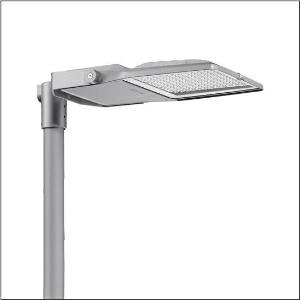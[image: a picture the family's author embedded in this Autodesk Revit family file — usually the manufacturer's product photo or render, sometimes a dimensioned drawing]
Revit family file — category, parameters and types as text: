
# Revit family: floodlight_fl_21_iq_midi___pl33t_5xa7782e2f3a_552b
name_source: partatom
category: Lighting Fixtures
units: mm (PartAtom-declared; Revit-internal decimal feet)

## family parameters
Cut with Voids When Loaded = No
Host = Face
Light Source = No
Part Type = Normal
Room Calculation Point = No
Round Connector Dimension = Use Diameter
Shared = No

## types (1)
- --- (1 x LED, 26540 lm, 208.1 W, 3000K)
    Apparent Load = 208 VA
    CIE Flux Codes = 26 75 99 100 100
    Color Rendering = 70
    Color Temperature = 3000K
    Default Elevation = 1800 mm
    Description = Floodlight FL 21 iQ midi, floodlight, primary light control with lens, of PMMA, primary optical cover: protective disc, of toughened safety glass, transparent, light distribution: PL33T, light emission: direct distribution, installation type: surface-mounted, LED, High Power LED, rated luminous flux: 26.540lm, luminous efficacy: 128lm/W, light colour: 730, colour temperature: 3000K, control gear: ECG iQ, control: optimised constant luminous flux control (CLO 2.0), Desk-Remote (wireless, voltage-free reading and setting of iQ features in the workshop via application-optimized NFC function/RFID function), Smart-Wire, Night-Set, Temp-Guard, Auto-Match, Street-Remote, with terminal, 6-pole, mains connection: 220..240V, AC, 50/60Hz, start of lifetime: 208W, end of service life: 227W, reduction: 90W, luminaire housing, of diecast aluminium, powder-coated, Siteco® metallic grey (DB 702S), corrosivity category C5 mid according to DIN EN ISO 12944, sealing non-destructively replaceable, please order mast flange separately, mast bracket, of steel, galvanised, powder-coated, Siteco® metallic grey (DB 702S), protection rating (complete): IP66, insulation class (complete): insulation class II (safety insulation), certification: CE, protection symbol: D, impact resistance: IK08, permissible operating ambient temperature: -40..+40°C, permissible operating ambient temperature for outdoor applications: -40..+50°C, standard: DIN EN 12944, LABS conformity tested according to VDMA 24364:2018-05, packaging unit: 1 piece

Light Distribution: PL33T
    Height = 76 mm
    Lamp = 1 x LED
    Lamp Light Flux = 26540 lm
    Lamp Power = 208.1 W
    Lamp count = 1
    Length = 657 mm
    Luminous efficacy = 128 lm/W
    Manufacturer = Siteco
    ModVariant = No
    Model = 5XA7782E2F3A
    Number of Poles = 1
    OnlyDefault = Yes
    Power Factor = 1
    Product Name = Floodlight FL 21 iQ midi | PL33T
    Product group = floodlight | pylon annexe
    ProductGroupID = 6200
    Protection Class = Protection class II
    Protection Degree = IP 66
    RLX_Detail_Level = 1
    RLX_Emergency_Light_Flux = 0 lm
    RLX_Emergency_Type = 0
    RLX_Emergency_Type_DB = No
    RlxData = <blob elided: 153657 chars, md5=505e4477>
    Socket = socket
    Standby Power = 0 W
    System Light Flux = 26540 lm
    System Power = 208 W
    Type Comments = factory setting: luminous flux: 100 % | dim-lin: 254 | 710 mA
    Type Image = l_1007123.jpg
    URL = http://relux.com
    VarID = @adj_052115
    Voltage = 0 V
    Weight = 0.00 kg
    Width = 442 mm

## geometry (parser evidence)
native form markers: Blend x4, Sweep x14
no freeform markers — native parametric forms only
